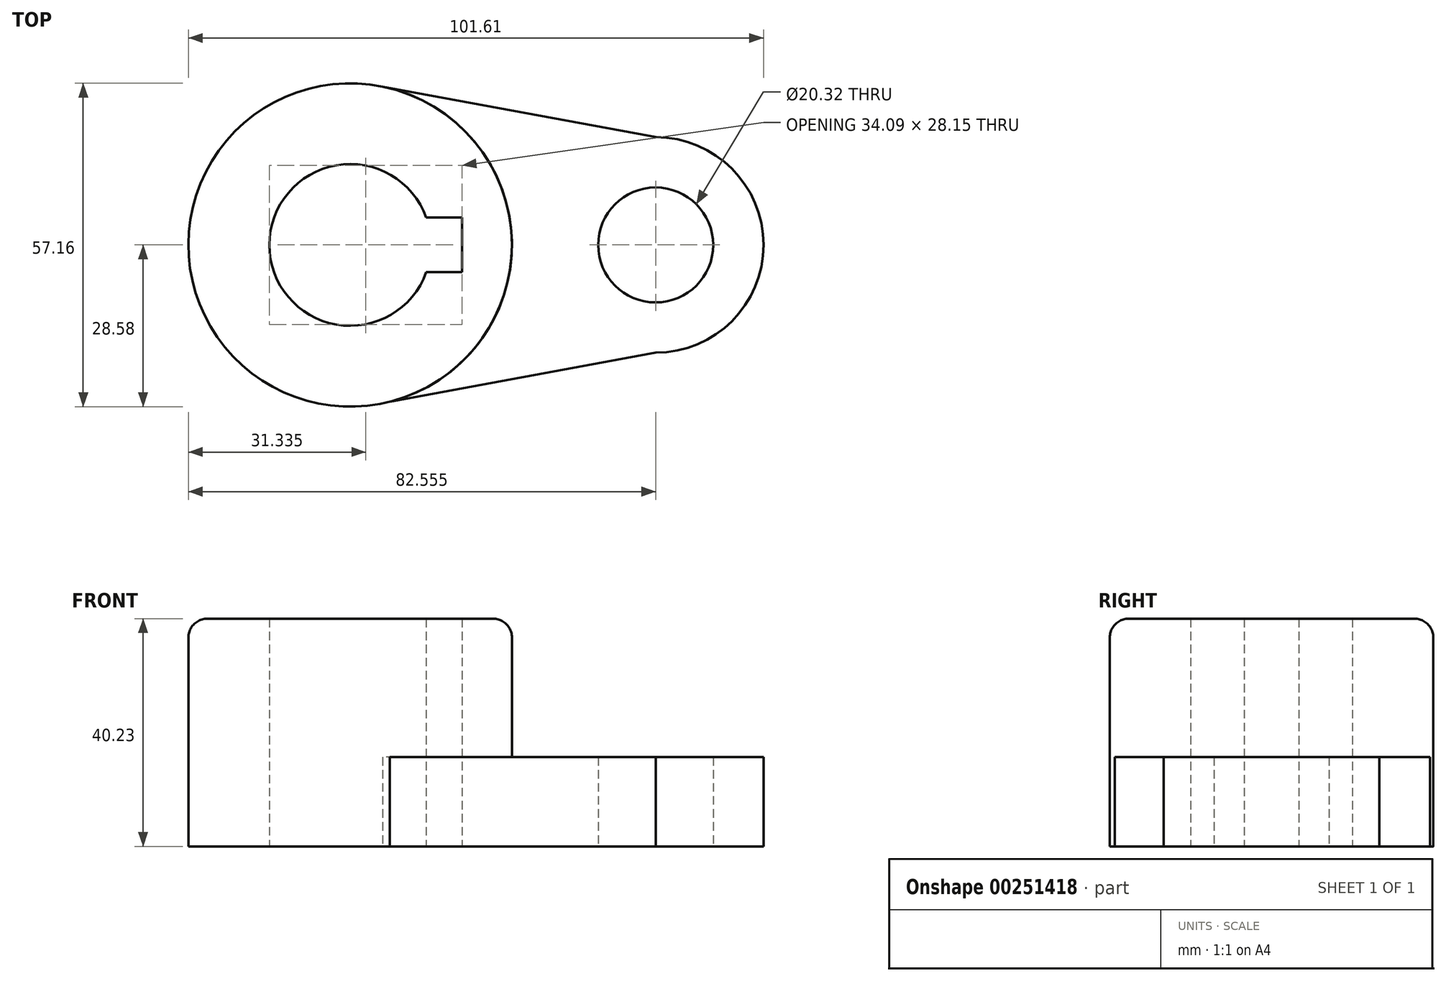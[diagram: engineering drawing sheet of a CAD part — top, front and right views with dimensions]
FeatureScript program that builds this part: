
annotation { "Feature Type Name" : "Feature", "Feature Type Description" : "" }
export const myFeature = defineFeature(function(context is Context, id is Id, definition is map)
    precondition{}
    {
        {
            var Q0;
            Q0=qCreatedBy(makeId("Top.planeOp"),FACE);
            var sketch = newSketch(context, id + "F0", { "sketchPlane" : qUnion([Q0])});
            skCircle(sketch, "E0", {"center": v(53.98, 0) * mm, "radius": 10.16 * mm});
            skCircle(sketch, "E1", {"center": v(0, 0) * mm, "radius": 28.58 * mm});
            skCircle(sketch, "E2", {"center": v(53.98, 0) * mm, "radius": 19.05 * mm});
            skPoint(sketch, "E3.visualSharp", {"position": v(33.04, -28.58) * mm});
            skCircle(sketch, "E4", {"center": v(0, 0) * mm, "radius": 14.29 * mm});
            skLineSegment(sketch, "E5", {"start": v(13.45, 4.83) * mm, "end": v(19.8, 4.83) * mm});
            skLineSegment(sketch, "E6", {"start": v(19.8, 4.83) * mm, "end": v(19.8, -4.83) * mm});
            skLineSegment(sketch, "E7", {"start": v(19.8, -4.83) * mm, "end": v(13.45, -4.83) * mm});
            skLineSegment(sketch, "E8", {"start": v(53.98, 19.05) * mm, "end": v(5.74, 28) * mm});
            skLineSegment(sketch, "E9", {"start": v(53.97, -19.05) * mm, "end": v(6.98, -27.7) * mm});
            skSolve(sketch);
        }
        {
            var Q0;
            Q0=makeQuery(id+"F0.imprint","IMPRINT",FACE,{"disambiguationData":[TD([[makeQuery(id+"F0.imprint","IMPRINT",EDGE,{"derivedFrom":sQuery(id+"F0.wireOp",EDGE,"OW2BRuVo-h5eh-Ojls-tUQz-FdrJ9uoOWhWJ")}),-1.0]])]});
            var Q1;
            {var subQ0=sQuery(id+"F0.wireOp",EDGE,"E5");Q1=makeQuery(id+"F0.imprint","IMPRINT",FACE,{"disambiguationData":[TD([[makeQuery(id+"F0.imprint","IMPRINT",EDGE,{"derivedFrom":subQ0}),1.0]])]});}
            extrude(context, id + "F1", {"entities" : qUnion([Q0, Q1]), "depth" : 40.23 * mm});
        }
        {
            var Q0;
            {var subQ0=sQuery(id+"F0.wireOp",EDGE,"o5OdITKO-bEnJ-2VYi-a7Jk-zIUuU5JH3HSI");var subQ1=sQuery(id+"F0.wireOp",EDGE,"E1");var subQ2=makeQuery(id+"F0.imprint","INTERSECT",VERTEX,{"disambiguationData":[OD(1.0)],"derivedFrom":[subQ1,subQ0]});Q0=makeQuery(id+"F0.imprint","IMPRINT",FACE,{"disambiguationData":[TD([[makeQuery(id+"F0.imprint","IMPRINT",EDGE,{"disambiguationData":[TD([[subQ2,1.0]])],"derivedFrom":subQ1}),-1.0]])]});}
            var Q1;
            Q1=makeQuery(id+"F0.imprint","IMPRINT",FACE,{"disambiguationData":[TD([[makeQuery(id+"F0.imprint","IMPRINT",EDGE,{"derivedFrom":sQuery(id+"F0.wireOp",EDGE,"E0")}),-1.0]])]});
            extrude(context, id + "F2", {"entities" : qUnion([Q0, Q1]), "operationType" : NewBodyOperationType.ADD, "depth" : 15.77 * mm});
        }
        {
            var Q0;
            {var subQ0=sQuery(id+"F0.wireOp",EDGE,"E1");Q0=makeQuery(id+"F1.opExtrude","CAP_EDGE",EDGE,{"disambiguationData":[OSD([subQ0]),TDD([makeQuery(id+"F0.imprint","IMPRINT",EDGE,{"disambiguationData":[TD([[makeQuery(id+"F0.imprint","INTERSECT",VERTEX,{"disambiguationData":[OD(0.0)],"derivedFrom":[subQ0,sQuery(id+"F0.wireOp",EDGE,"SRnHb5uK-vhAm-8B8o-SrwD-EHZrL22LgCVp")]}),1.0]])],"derivedFrom":subQ0})])],"isStart":false});}
            var Q1;
            Q1=makeQuery(id+"F1.opExtrude","CAP_EDGE",EDGE,{"disambiguationData":[OSD([sQuery(id+"F0.wireOp",EDGE,"SRnHb5uK-vhAm-8B8o-SrwD-EHZrL22LgCVp")])],"isStart":false});
            var Q2;
            {var subQ0=sQuery(id+"F0.wireOp",EDGE,"E1");Q2=makeQuery(id+"F1.opExtrude","CAP_EDGE",EDGE,{"disambiguationData":[OSD([subQ0]),TDD([makeQuery(id+"F0.imprint","IMPRINT",EDGE,{"disambiguationData":[TD([[makeQuery(id+"F0.imprint","INTERSECT",VERTEX,{"disambiguationData":[OD(1.0)],"derivedFrom":[subQ0,sQuery(id+"F0.wireOp",EDGE,"o5OdITKO-bEnJ-2VYi-a7Jk-zIUuU5JH3HSI")]}),1.0]])],"derivedFrom":subQ0})])],"isStart":false});}
            var Q3;
            Q3=makeQuery(id+"F1.opExtrude","CAP_EDGE",EDGE,{"disambiguationData":[OSD([sQuery(id+"F0.wireOp",EDGE,"o5OdITKO-bEnJ-2VYi-a7Jk-zIUuU5JH3HSI")])],"isStart":false});
            fillet(context, id + "F3", {"entities" : qUnion([Q0, Q1, Q2, Q3]), "radius" : 3.3 * mm, "tangentPropagation" : true, "allowEdgeOverflow" : false});
        }
    });
